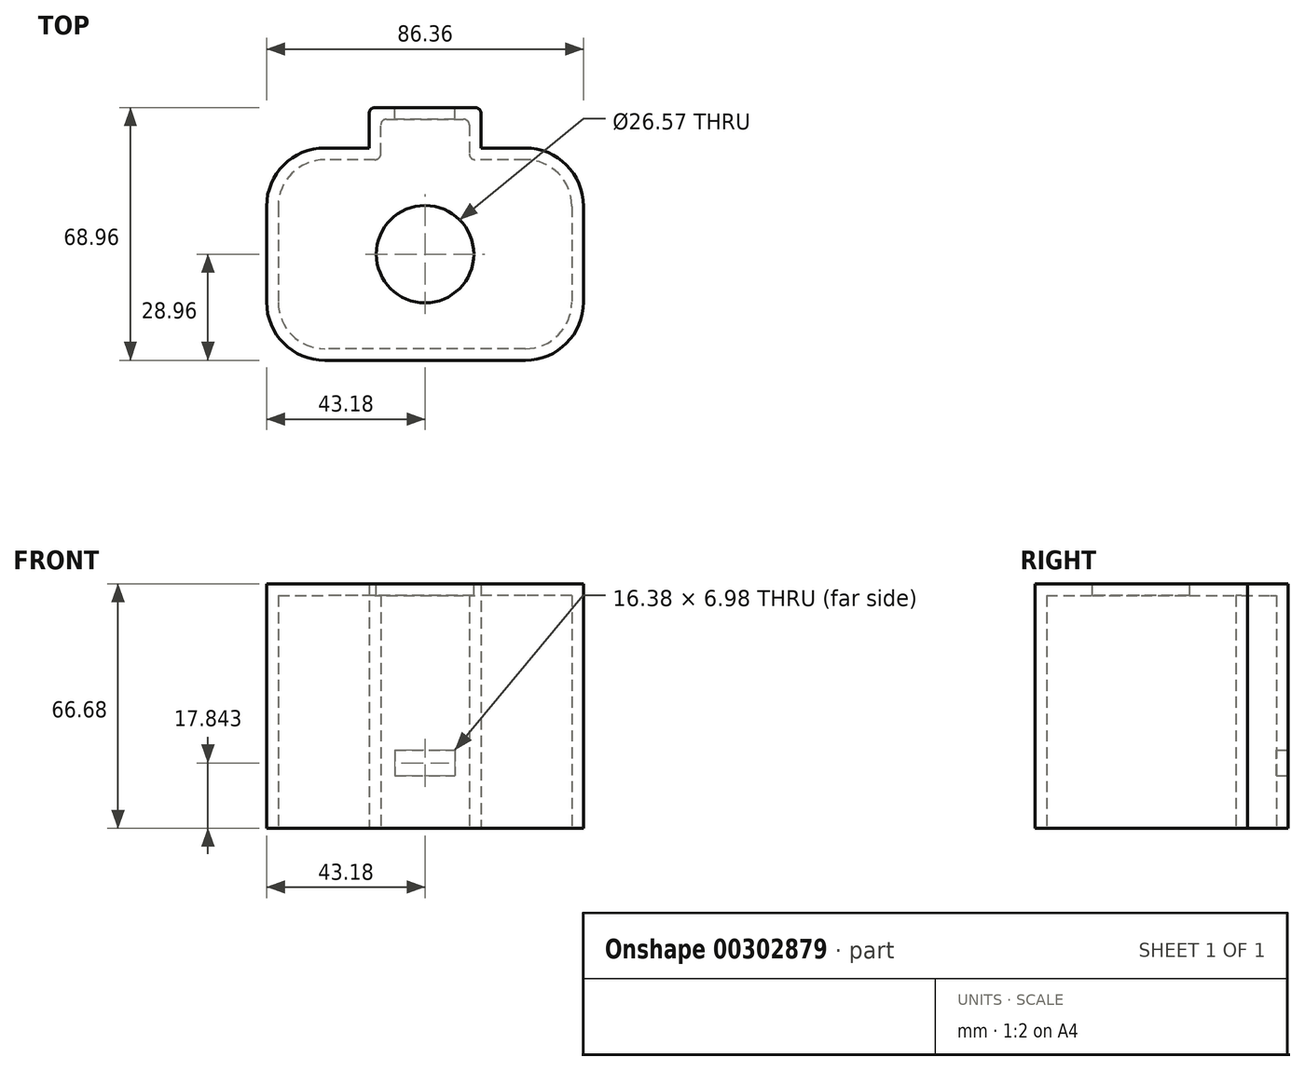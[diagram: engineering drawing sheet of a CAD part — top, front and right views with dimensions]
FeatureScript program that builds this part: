
annotation { "Feature Type Name" : "Feature", "Feature Type Description" : "" }
export const myFeature = defineFeature(function(context is Context, id is Id, definition is map)
    precondition{}
    {
        {
            var Q0;
            Q0=qCreatedBy(makeId("Top.planeOp"),FACE);
            var sketch = newSketch(context, id + "F0", { "sketchPlane" : qUnion([Q0])});
            skLineSegment(sketch, "E0.bottom", {"start": v(27.3, 25.78) * mm, "end": v(12.07, 25.78) * mm});
            skLineSegment(sketch, "E0.top", {"start": v(27.3, -25.78) * mm, "end": v(-27.3, -25.78) * mm});
            skLineSegment(sketch, "E0.left", {"start": v(40, 13.08) * mm, "end": v(40, -13.08) * mm});
            skLineSegment(sketch, "E0.right", {"start": v(-40, 13.08) * mm, "end": v(-40, -13.08) * mm});
            skPoint(sketch, "E0.middle", {"position": v(0, 0) * mm});
            skPoint(sketch, "E1.visualSharp", {"position": v(-40, -25.78) * mm});
            skArc(sketch, "E1.filletArc", {"start": v(-40, -13.08) * mm, "mid": v(-36.29, -22.06) * mm, "end": v(-27.3, -25.78) * mm});
            skPoint(sketch, "E2.visualSharp", {"position": v(-40, 25.78) * mm});
            skArc(sketch, "E2.filletArc", {"start": v(-27.3, 25.78) * mm, "mid": v(-36.29, 22.06) * mm, "end": v(-40, 13.08) * mm});
            skPoint(sketch, "E3.visualSharp", {"position": v(40, 25.78) * mm});
            skArc(sketch, "E3.filletArc", {"start": v(40, 13.08) * mm, "mid": v(36.29, 22.06) * mm, "end": v(27.3, 25.78) * mm});
            skPoint(sketch, "E4.visualSharp", {"position": v(40, -25.78) * mm});
            skArc(sketch, "E4.filletArc", {"start": v(27.3, -25.78) * mm, "mid": v(36.29, -22.06) * mm, "end": v(40, -13.08) * mm});
            skLineSegment(sketch, "E5", {"start": v(-12.06, 25.78) * mm, "end": v(-12.07, 36.83) * mm});
            skLineSegment(sketch, "E6", {"start": v(-12.07, 36.83) * mm, "end": v(12.06, 36.83) * mm});
            skLineSegment(sketch, "E7", {"start": v(12.06, 36.83) * mm, "end": v(12.07, 25.78) * mm});
            skLineSegment(sketch, "E8.trimOffspring", {"start": v(-12.06, 25.78) * mm, "end": v(-27.3, 25.78) * mm});
            skLineSegment(sketch, "E9.0", {"start": v(-15.24, 28.96) * mm, "end": v(-27.3, 28.96) * mm});
            skArc(sketch, "E9.1", {"start": v(27.3, -28.96) * mm, "mid": v(38.53, -24.3) * mm, "end": v(43.18, -13.08) * mm});
            skLineSegment(sketch, "E9.2", {"start": v(27.3, -28.96) * mm, "end": v(-27.3, -28.96) * mm});
            skArc(sketch, "E9.3", {"start": v(-43.18, -13.08) * mm, "mid": v(-38.53, -24.3) * mm, "end": v(-27.3, -28.96) * mm});
            skLineSegment(sketch, "E9.4", {"start": v(-43.18, 13.08) * mm, "end": v(-43.18, -13.08) * mm});
            skLineSegment(sketch, "E9.5", {"start": v(43.18, 13.08) * mm, "end": v(43.18, -13.08) * mm});
            skArc(sketch, "E9.6", {"start": v(-27.3, 28.96) * mm, "mid": v(-38.53, 24.3) * mm, "end": v(-43.18, 13.08) * mm});
            skArc(sketch, "E9.7", {"start": v(43.18, 13.08) * mm, "mid": v(38.53, 24.3) * mm, "end": v(27.3, 28.96) * mm});
            skLineSegment(sketch, "E9.8", {"start": v(27.3, 28.96) * mm, "end": v(15.24, 28.96) * mm});
            skLineSegment(sketch, "E9.9", {"start": v(15.24, 40) * mm, "end": v(15.24, 28.96) * mm});
            skLineSegment(sketch, "E9.10", {"start": v(-15.24, 40) * mm, "end": v(15.24, 40) * mm});
            skLineSegment(sketch, "E9.11", {"start": v(-15.24, 28.96) * mm, "end": v(-15.24, 40) * mm});
            skSolve(sketch);
        }
        {
            var Q0;
            Q0=qSketchRegion(id+"F0",true);
            extrude(context, id + "F1", {"entities" : qUnion([Q0]), "depth" : 63.5 * mm});
        }
        {
            var Q0;
            Q0=makeQuery(id+"F1.opExtrude","SWEPT_FACE",FACE,{"disambiguationData":[OSD([sQuery(id+"F0.wireOp",EDGE,"E9.10")])]});
            var sketch = newSketch(context, id + "F2", { "sketchPlane" : qUnion([Q0])});
            skLineSegment(sketch, "E10.bottom", {"start": v(8.2, 21.34) * mm, "end": v(-8.2, 21.34) * mm});
            skLineSegment(sketch, "E10.top", {"start": v(8.2, 14.35) * mm, "end": v(-8.2, 14.35) * mm});
            skLineSegment(sketch, "E10.left", {"start": v(8.2, 21.34) * mm, "end": v(8.2, 14.35) * mm});
            skLineSegment(sketch, "E10.right", {"start": v(-8.2, 21.34) * mm, "end": v(-8.2, 14.35) * mm});
            skPoint(sketch, "E10.middle", {"position": v(0, 17.84) * mm});
            skSolve(sketch);
        }
        {
            var Q0;
            Q0=qSketchRegion(id+"F2",true);
            extrude(context, id + "F3", {"entities" : qUnion([Q0]), "operationType" : NewBodyOperationType.REMOVE, "endBound" : BoundingType.UP_TO_NEXT, "oppositeDirection" : true, "depth" : 25.4 * mm});
        }
        {
            var Q0;
            Q0=makeQuery(id+"F1.opExtrude","SWEPT_EDGE",EDGE,{"disambiguationData":[OSD([sQuery(id+"F0.wireOp",EDGE,"E5"),sQuery(id+"F0.wireOp",EDGE,"E8.trimOffspring")])]});
            var Q1;
            Q1=makeQuery(id+"F1.opExtrude","SWEPT_EDGE",EDGE,{"disambiguationData":[OSD([sQuery(id+"F0.wireOp",EDGE,"E5"),sQuery(id+"F0.wireOp",EDGE,"E6")])]});
            var Q2;
            Q2=makeQuery(id+"F1.opExtrude","SWEPT_EDGE",EDGE,{"disambiguationData":[OSD([sQuery(id+"F0.wireOp",EDGE,"E0.bottom"),sQuery(id+"F0.wireOp",EDGE,"E7")])]});
            var Q3;
            Q3=makeQuery(id+"F1.opExtrude","SWEPT_EDGE",EDGE,{"disambiguationData":[OSD([sQuery(id+"F0.wireOp",EDGE,"E6"),sQuery(id+"F0.wireOp",EDGE,"E7")])]});
            var Q4;
            Q4=makeQuery(id+"F1.opExtrude","SWEPT_EDGE",EDGE,{"disambiguationData":[OSD([sQuery(id+"F0.wireOp",EDGE,"E9.9"),sQuery(id+"F0.wireOp",EDGE,"E9.10")])]});
            var Q5;
            Q5=makeQuery(id+"F1.opExtrude","SWEPT_EDGE",EDGE,{"disambiguationData":[OSD([sQuery(id+"F0.wireOp",EDGE,"E9.10"),sQuery(id+"F0.wireOp",EDGE,"E9.11")])]});
            fillet(context, id + "F4", {"entities" : qUnion([Q0, Q1, Q2, Q3, Q4, Q5]), "radius" : 1.59 * mm, "tangentPropagation" : true, "allowEdgeOverflow" : false});
        }
        {
            var Q0;
            Q0=makeQuery(id+"F1.opExtrude","CAP_FACE",FACE,{"disambiguationData":[OSD([sQuery(id+"F0.wireOp",EDGE,"E0.bottom"),sQuery(id+"F0.wireOp",EDGE,"E0.top"),sQuery(id+"F0.wireOp",EDGE,"E0.left"),sQuery(id+"F0.wireOp",EDGE,"E0.right"),sQuery(id+"F0.wireOp",EDGE,"E1.filletArc"),sQuery(id+"F0.wireOp",EDGE,"E2.filletArc"),sQuery(id+"F0.wireOp",EDGE,"E3.filletArc"),sQuery(id+"F0.wireOp",EDGE,"E4.filletArc"),sQuery(id+"F0.wireOp",EDGE,"E5"),sQuery(id+"F0.wireOp",EDGE,"E6"),sQuery(id+"F0.wireOp",EDGE,"E7"),sQuery(id+"F0.wireOp",EDGE,"E8.trimOffspring"),sQuery(id+"F0.wireOp",EDGE,"E9.0"),sQuery(id+"F0.wireOp",EDGE,"E9.1"),sQuery(id+"F0.wireOp",EDGE,"E9.2"),sQuery(id+"F0.wireOp",EDGE,"E9.3"),sQuery(id+"F0.wireOp",EDGE,"E9.4"),sQuery(id+"F0.wireOp",EDGE,"E9.5"),sQuery(id+"F0.wireOp",EDGE,"E9.6"),sQuery(id+"F0.wireOp",EDGE,"E9.7"),sQuery(id+"F0.wireOp",EDGE,"E9.8"),sQuery(id+"F0.wireOp",EDGE,"E9.9"),sQuery(id+"F0.wireOp",EDGE,"E9.10"),sQuery(id+"F0.wireOp",EDGE,"E9.11")])],"isStart":false});
            var sketch = newSketch(context, id + "F5", { "sketchPlane" : qUnion([Q0])});
            skArc(sketch, "E11.0", {"start": v(-13.65, 40) * mm, "mid": v(-14.78, 39.54) * mm, "end": v(-15.24, 38.42) * mm});
            skArc(sketch, "E11.1", {"start": v(15.24, 38.42) * mm, "mid": v(14.78, 39.54) * mm, "end": v(13.65, 40) * mm});
            skLineSegment(sketch, "E11.2", {"start": v(15.24, 38.42) * mm, "end": v(15.24, 28.96) * mm});
            skLineSegment(sketch, "E11.3", {"start": v(-13.65, 40) * mm, "end": v(13.65, 40) * mm});
            skLineSegment(sketch, "E11.4", {"start": v(-15.24, 28.96) * mm, "end": v(-15.24, 38.42) * mm});
            skLineSegment(sketch, "E11.5", {"start": v(-15.24, 28.96) * mm, "end": v(-27.3, 28.96) * mm});
            skArc(sketch, "E11.6", {"start": v(-27.3, 28.96) * mm, "mid": v(-38.53, 24.3) * mm, "end": v(-43.18, 13.08) * mm});
            skLineSegment(sketch, "E11.7", {"start": v(27.3, 28.96) * mm, "end": v(15.24, 28.96) * mm});
            skArc(sketch, "E11.8", {"start": v(43.18, 13.08) * mm, "mid": v(38.53, 24.3) * mm, "end": v(27.3, 28.96) * mm});
            skLineSegment(sketch, "E11.9", {"start": v(-43.18, 13.08) * mm, "end": v(-43.18, -13.08) * mm});
            skArc(sketch, "E11.10", {"start": v(-43.18, -13.08) * mm, "mid": v(-38.53, -24.3) * mm, "end": v(-27.3, -28.96) * mm});
            skLineSegment(sketch, "E11.11", {"start": v(27.3, -28.96) * mm, "end": v(-27.3, -28.96) * mm});
            skArc(sketch, "E11.12", {"start": v(27.3, -28.96) * mm, "mid": v(38.53, -24.3) * mm, "end": v(43.18, -13.08) * mm});
            skLineSegment(sketch, "E11.13", {"start": v(43.18, 13.08) * mm, "end": v(43.18, -13.08) * mm});
            skSolve(sketch);
        }
        {
            var Q0;
            Q0 = qSketchRegion(id + "F5", true);
            extrude(context, id + "F6", {"entities" : qUnion([Q0]), "operationType" : NewBodyOperationType.ADD, "depth" : 3.17 * mm});
        }
        {
            var Q0;
            Q0=makeQuery(id+"F6.opExtrude","CAP_FACE",FACE,{"disambiguationData":[OSD([sQuery(id+"F5.wireOp",EDGE,"E11.0"),sQuery(id+"F5.wireOp",EDGE,"E11.1"),sQuery(id+"F5.wireOp",EDGE,"E11.2"),sQuery(id+"F5.wireOp",EDGE,"E11.3"),sQuery(id+"F5.wireOp",EDGE,"E11.4"),sQuery(id+"F5.wireOp",EDGE,"E11.5"),sQuery(id+"F5.wireOp",EDGE,"E11.6"),sQuery(id+"F5.wireOp",EDGE,"E11.7"),sQuery(id+"F5.wireOp",EDGE,"E11.8"),sQuery(id+"F5.wireOp",EDGE,"E11.9"),sQuery(id+"F5.wireOp",EDGE,"E11.10"),sQuery(id+"F5.wireOp",EDGE,"E11.11"),sQuery(id+"F5.wireOp",EDGE,"E11.12"),sQuery(id+"F5.wireOp",EDGE,"E11.13")])],"isStart":false});
            var sketch = newSketch(context, id + "F7", { "sketchPlane" : qUnion([Q0])});
            skCircle(sketch, "E12", {"center": v(0, 0) * mm, "radius": 13.28 * mm});
            skSolve(sketch);
        }
        {
            var Q0;
            Q0 = qSketchRegion(id + "F7", true);
            extrude(context, id + "F8", {"entities" : qUnion([Q0]), "operationType" : NewBodyOperationType.REMOVE, "endBound" : BoundingType.UP_TO_NEXT, "oppositeDirection" : true, "depth" : 25.4 * mm});
        }
        {
            var Q0;
            Q0=makeQuery(id+"F1.opExtrude","SWEPT_BODY",BODY,{"disambiguationData":[OSD([sQuery(id+"F0.wireOp",EDGE,"E0.bottom"),sQuery(id+"F0.wireOp",EDGE,"E0.top"),sQuery(id+"F0.wireOp",EDGE,"E0.left"),sQuery(id+"F0.wireOp",EDGE,"E0.right"),sQuery(id+"F0.wireOp",EDGE,"E1.filletArc"),sQuery(id+"F0.wireOp",EDGE,"E2.filletArc"),sQuery(id+"F0.wireOp",EDGE,"E3.filletArc"),sQuery(id+"F0.wireOp",EDGE,"E4.filletArc"),sQuery(id+"F0.wireOp",EDGE,"E5"),sQuery(id+"F0.wireOp",EDGE,"E6"),sQuery(id+"F0.wireOp",EDGE,"E7"),sQuery(id+"F0.wireOp",EDGE,"E8.trimOffspring"),sQuery(id+"F0.wireOp",EDGE,"E9.0"),sQuery(id+"F0.wireOp",EDGE,"E9.1"),sQuery(id+"F0.wireOp",EDGE,"E9.2"),sQuery(id+"F0.wireOp",EDGE,"E9.3"),sQuery(id+"F0.wireOp",EDGE,"E9.4"),sQuery(id+"F0.wireOp",EDGE,"E9.5"),sQuery(id+"F0.wireOp",EDGE,"E9.6"),sQuery(id+"F0.wireOp",EDGE,"E9.7"),sQuery(id+"F0.wireOp",EDGE,"E9.8"),sQuery(id+"F0.wireOp",EDGE,"E9.9"),sQuery(id+"F0.wireOp",EDGE,"E9.10"),sQuery(id+"F0.wireOp",EDGE,"E9.11")])]});
            transform(context, id + "F9", {"entities" : qUnion([Q0]), "transformType" : TransformType.TRANSLATION_3D, "dx" : 0 * mm, "dy" : 0 * mm, "dz" : 0 * mm, "makeCopy" : true});
        }
        {
            var Q0;
            Q0=makeQuery(id+"F9.opPattern","COPY",BODY,{"derivedFrom":makeQuery(id+"F1.opExtrude","SWEPT_BODY",BODY,{"disambiguationData":[OSD([sQuery(id+"F0.wireOp",EDGE,"E0.bottom"),sQuery(id+"F0.wireOp",EDGE,"E0.top"),sQuery(id+"F0.wireOp",EDGE,"E0.left"),sQuery(id+"F0.wireOp",EDGE,"E0.right"),sQuery(id+"F0.wireOp",EDGE,"E1.filletArc"),sQuery(id+"F0.wireOp",EDGE,"E2.filletArc"),sQuery(id+"F0.wireOp",EDGE,"E3.filletArc"),sQuery(id+"F0.wireOp",EDGE,"E4.filletArc"),sQuery(id+"F0.wireOp",EDGE,"E5"),sQuery(id+"F0.wireOp",EDGE,"E6"),sQuery(id+"F0.wireOp",EDGE,"E7"),sQuery(id+"F0.wireOp",EDGE,"E8.trimOffspring"),sQuery(id+"F0.wireOp",EDGE,"E9.0"),sQuery(id+"F0.wireOp",EDGE,"E9.1"),sQuery(id+"F0.wireOp",EDGE,"E9.2"),sQuery(id+"F0.wireOp",EDGE,"E9.3"),sQuery(id+"F0.wireOp",EDGE,"E9.4"),sQuery(id+"F0.wireOp",EDGE,"E9.5"),sQuery(id+"F0.wireOp",EDGE,"E9.6"),sQuery(id+"F0.wireOp",EDGE,"E9.7"),sQuery(id+"F0.wireOp",EDGE,"E9.8"),sQuery(id+"F0.wireOp",EDGE,"E9.9"),sQuery(id+"F0.wireOp",EDGE,"E9.10"),sQuery(id+"F0.wireOp",EDGE,"E9.11")])]}),"instanceName":"1"});
            deleteBodies(context, id + "F10", {"entities" : qUnion([Q0])});
        }
    });
